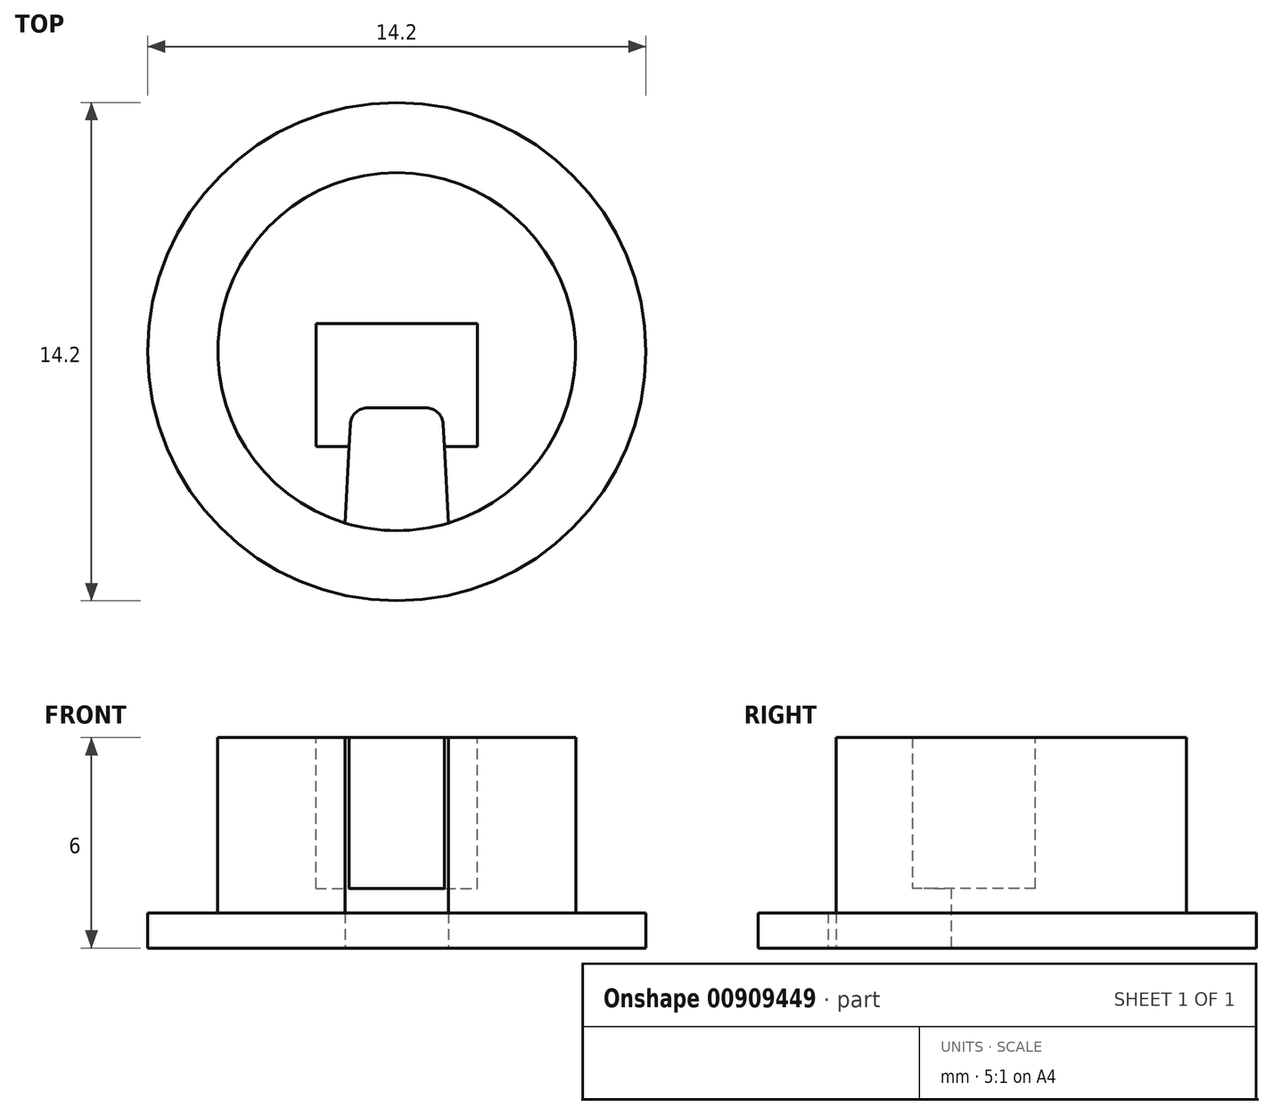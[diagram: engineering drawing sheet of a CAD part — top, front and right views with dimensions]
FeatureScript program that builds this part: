
annotation { "Feature Type Name" : "Feature", "Feature Type Description" : "" }
export const myFeature = defineFeature(function(context is Context, id is Id, definition is map)
    precondition{}
    {
        {
            var Q0;
            Q0=qCreatedBy(makeId("Top.planeOp"),FACE);
            var sketch = newSketch(context, id + "F0", { "sketchPlane" : qUnion([Q0])});
            skCircle(sketch, "E0", {"center": v(0, 0) * mm, "radius": 5.1 * mm});
            skLineSegment(sketch, "E1", {"start": v(-1.3, -4.93) * mm, "end": v(-1.3, -1.6) * mm});
            skLineSegment(sketch, "E2", {"start": v(-1.3, -1.6) * mm, "end": v(1.3, -1.6) * mm});
            skLineSegment(sketch, "E3", {"start": v(1.3, -1.6) * mm, "end": v(1.3, -4.93) * mm});
            skCircle(sketch, "E4", {"center": v(0, 0) * mm, "radius": 7.1 * mm});
            skLineSegment(sketch, "E5", {"start": v(1.3, -1.6) * mm, "end": v(1.47, -4.88) * mm});
            skLineSegment(sketch, "E6", {"start": v(-1.3, -1.6) * mm, "end": v(-1.47, -4.88) * mm});
            skSolve(sketch);
        }
        {
            var Q0;
            Q0 = qSketchRegion(id + "F0", true);
            extrude(context, id + "F1", {"entities" : qUnion([Q0]), "depth" : 1 * mm, "offsetDistance" : 25 * mm});
        }
        {
            var Q0;
            Q0=makeQuery(id+"F0.imprint","IMPRINT",FACE,{"disambiguationData":[TD([[makeQuery(id+"F0.imprint","IMPRINT",EDGE,{"derivedFrom":sQuery(id+"F0.wireOp",EDGE,"E2")}),1.0]])]});
            extrude(context, id + "F2", {"entities" : qUnion([Q0]), "operationType" : NewBodyOperationType.ADD, "depth" : 6 * mm, "offsetDistance" : 25 * mm});
        }
        {
            var Q0;
            Q0=makeQuery(id+"F2.opExtrude","SWEPT_EDGE",EDGE,{"disambiguationData":[OSD([sQuery(id+"F0.wireOp",EDGE,"E1"),sQuery(id+"F0.wireOp",EDGE,"E2")])]});
            var Q1;
            Q1=makeQuery(id+"F2.opExtrude","SWEPT_EDGE",EDGE,{"disambiguationData":[OSD([sQuery(id+"F0.wireOp",EDGE,"E2"),sQuery(id+"F0.wireOp",EDGE,"E3")])]});
            fillet(context, id + "F3", {"entities" : qUnion([Q0, Q1]), "radius" : 0.5 * mm, "tangentPropagation" : true, "allowEdgeOverflow" : false});
        }
        {
            var Q0;
            Q0=makeQuery(id+"F2.opExtrude","CAP_FACE",FACE,{"disambiguationData":[OSD([sQuery(id+"F0.wireOp",EDGE,"E0"),sQuery(id+"F0.wireOp",EDGE,"E1"),sQuery(id+"F0.wireOp",EDGE,"E2"),sQuery(id+"F0.wireOp",EDGE,"E3")])],"isStart":false});
            cPlane(context, id + "F4", {"entities" : qUnion([Q0]), "cplaneType" : CPlaneType.OFFSET, "offset" : 0 * mm, "width" : 150 * mm, "height" : 150 * mm});
        }
        {
            var Q0;
            Q0=qCreatedBy(id+"F4.planeOp",FACE);
            var sketch = newSketch(context, id + "F5", { "sketchPlane" : qUnion([Q0])});
            skLineSegment(sketch, "E7.bottom", {"start": v(-2.3, 0.8) * mm, "end": v(2.3, 0.8) * mm});
            skLineSegment(sketch, "E7.top", {"start": v(-2.3, -2.7) * mm, "end": v(2.3, -2.7) * mm});
            skLineSegment(sketch, "E7.left", {"start": v(-2.3, 0.8) * mm, "end": v(-2.3, -2.7) * mm});
            skLineSegment(sketch, "E7.right", {"start": v(2.3, 0.8) * mm, "end": v(2.3, -2.7) * mm});
            skLineSegment(sketch, "E8.0", {"start": v(1.3, -2.25) * mm, "end": v(1.3, -4.57) * mm});
            skLineSegment(sketch, "E9.0", {"start": v(-1.3, -4.57) * mm, "end": v(-1.3, -2.25) * mm});
            skSolve(sketch);
        }
        {
            var Q0;
            Q0 = qSketchRegion(id + "F5", true);
            extrude(context, id + "F6", {"entities" : qUnion([Q0]), "operationType" : NewBodyOperationType.REMOVE, "oppositeDirection" : true, "depth" : 4.3 * mm, "offsetDistance" : 25 * mm});
        }
    });
